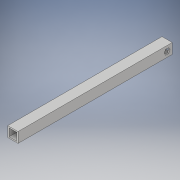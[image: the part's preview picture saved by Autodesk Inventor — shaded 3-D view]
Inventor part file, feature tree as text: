
AUTODESK INVENTOR PART (.ipt)
format: ipt  version: 2018 (Build 220112000, 112)  size: 115,200 bytes
history: native  units: in
note: dims shown in document units (in); Inventor stores cm internally (conversion verified against a paired STEP export)
features: extrude x2, sketch x2
ambient origin geometry x8: Origin, YZ Plane, XZ Plane, XY Plane, X Axis, Y Axis, Z Axis, Center Point
bodies: Solid1 (feature_tree)
feature tree (4):
  extrude  "Extrusion1"  Depth=1.0in
  extrude  "Extrusion2"  Depth=15.0in TaperAngle=0.0deg
  sketch  "Sketch1"  dims[d0=1.0in d1=1.0in]
  sketch  "Sketch2"  dims[d2=0.125in d3=15.0in d4=0.0in d5=0.5in d6=0.5in d7=15.0in d8=0.0in]
